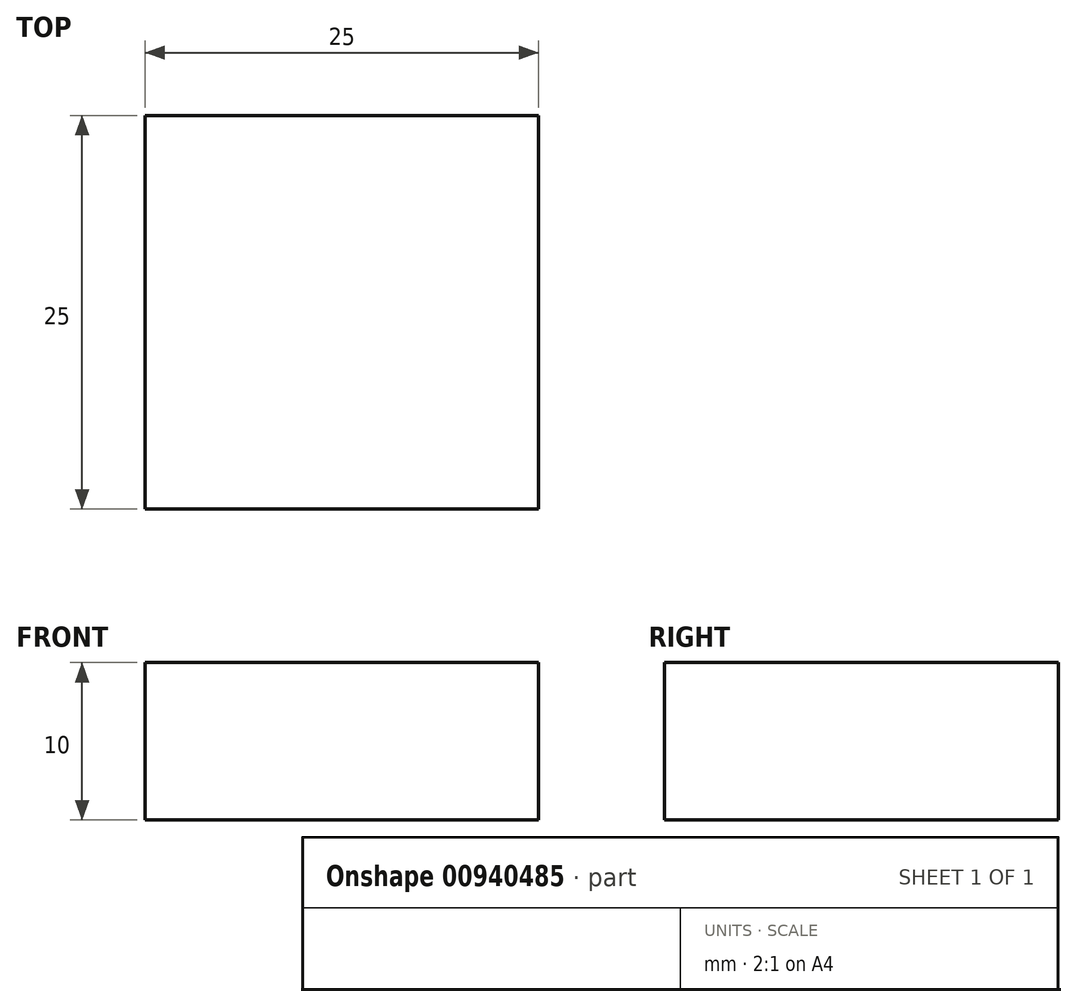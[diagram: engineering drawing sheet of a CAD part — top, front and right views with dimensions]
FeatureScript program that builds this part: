
annotation { "Feature Type Name" : "Feature", "Feature Type Description" : "" }
export const myFeature = defineFeature(function(context is Context, id is Id, definition is map)
    precondition{}
    {
        {
            var Q0;
            Q0=qCreatedBy(makeId("Top.planeOp"),FACE);
            var sketch = newSketch(context, id + "F0", { "sketchPlane" : qUnion([Q0])});
            skLineSegment(sketch, "E0", {"start": v(-25, 25) * mm, "end": v(-25, 0) * mm});
            skLineSegment(sketch, "E1", {"start": v(-25, 0) * mm, "end": v(0, 0) * mm});
            skLineSegment(sketch, "E2", {"start": v(-25, 25) * mm, "end": v(0, 25) * mm});
            skLineSegment(sketch, "E3", {"start": v(0, 25) * mm, "end": v(0, 0) * mm});
            skSolve(sketch);
        }
        {
            var Q0;
            Q0=makeQuery(id+"F0.imprint","IMPRINT",FACE,{"disambiguationData":[TD([[makeQuery(id+"F0.imprint","IMPRINT",EDGE,{"derivedFrom":sQuery(id+"F0.wireOp",EDGE,"E0")}),1.0]])]});
            extrude(context, id + "F1", {"entities" : qUnion([Q0]), "depth" : 25.4 * mm, "offsetDistance" : 25.4 * mm});
        }
        {
            var Q0;
            Q0=makeQuery(id+"F1.opExtrude","SWEPT_BODY",BODY,{"disambiguationData":[OSD([sQuery(id+"F0.wireOp",EDGE,"E0"),sQuery(id+"F0.wireOp",EDGE,"E1"),sQuery(id+"F0.wireOp",EDGE,"E2"),sQuery(id+"F0.wireOp",EDGE,"E3")])]});
            deleteBodies(context, id + "F2", {"entities" : qUnion([Q0])});
        }
        {
            var Q0;
            Q0=qCreatedBy(makeId("Top.planeOp"),FACE);
            var sketch = newSketch(context, id + "F3", { "sketchPlane" : qUnion([Q0])});
            skLineSegment(sketch, "E4.left", {"start": v(-50.94, 38.25) * mm, "end": v(-50.94, 38.75) * mm});
            skLineSegment(sketch, "E4.right", {"start": v(-69.3, 38.25) * mm, "end": v(-69.3, 38.75) * mm});
            skSolve(sketch);
        }
        {
            var Q0;
            Q0=makeQuery(id+"F0.imprint","IMPRINT",FACE,{"disambiguationData":[TD([[makeQuery(id+"F0.imprint","IMPRINT",EDGE,{"derivedFrom":sQuery(id+"F0.wireOp",EDGE,"E0")}),1.0]])]});
            var Q1;
            Q1 = qSketchRegion(id + "F3", true);
            extrude(context, id + "F4", {"entities" : qUnion([Q0, Q1]), "depth" : 10 * mm, "offsetDistance" : 25.4 * mm});
        }
    });
